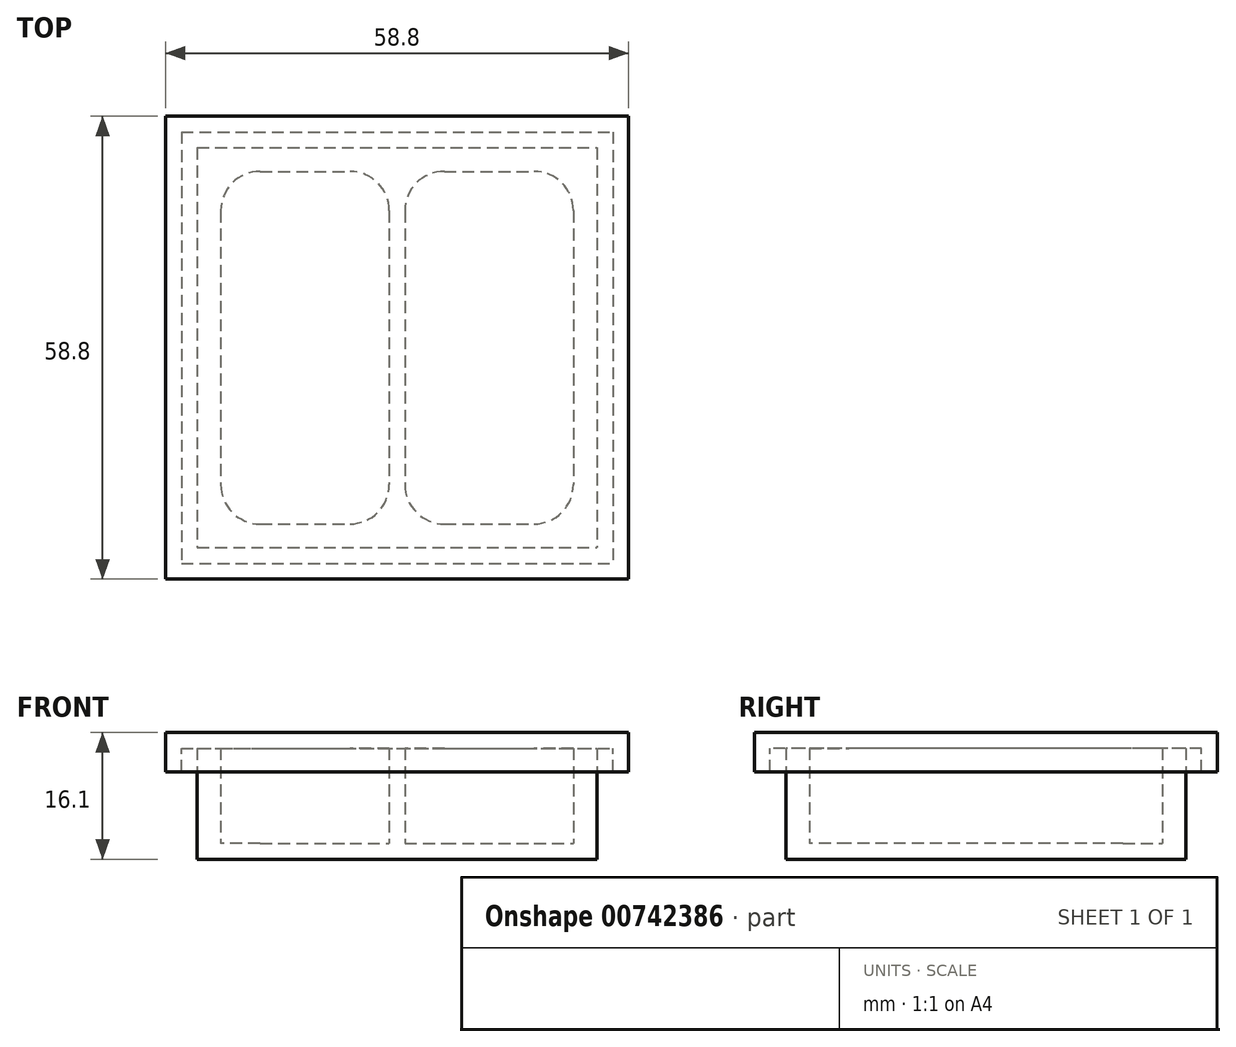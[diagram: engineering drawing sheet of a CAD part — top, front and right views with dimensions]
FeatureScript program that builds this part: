
annotation { "Feature Type Name" : "Feature", "Feature Type Description" : "" }
export const myFeature = defineFeature(function(context is Context, id is Id, definition is map)
    precondition{}
    {
        {
            var Q0;
            Q0=qCreatedBy(makeId("Top.planeOp"),FACE);
            var sketch = newSketch(context, id + "F0", { "sketchPlane" : qUnion([Q0])});
            skLineSegment(sketch, "E0.bottom", {"start": v(-30.87, 24.78) * mm, "end": v(19.93, 24.78) * mm});
            skLineSegment(sketch, "E0.top", {"start": v(-30.87, -26.02) * mm, "end": v(19.93, -26.02) * mm});
            skLineSegment(sketch, "E0.left", {"start": v(-30.87, 24.78) * mm, "end": v(-30.87, -26.02) * mm});
            skLineSegment(sketch, "E0.right", {"start": v(19.93, 24.78) * mm, "end": v(19.93, -26.02) * mm});
            skLineSegment(sketch, "E1.0", {"start": v(-27.87, 21.78) * mm, "end": v(16.93, 21.78) * mm});
            skLineSegment(sketch, "E1.1", {"start": v(-27.87, 21.78) * mm, "end": v(-27.87, 12.83) * mm});
            skLineSegment(sketch, "E1.2", {"start": v(-27.87, -23.02) * mm, "end": v(16.93, -23.02) * mm});
            skLineSegment(sketch, "E1.3", {"start": v(16.93, 21.78) * mm, "end": v(16.93, 12.83) * mm});
            skLineSegment(sketch, "E2", {"start": v(-6.47, -14.07) * mm, "end": v(-4.47, -14.07) * mm});
            skLineSegment(sketch, "E3", {"start": v(-6.47, -11.07) * mm, "end": v(-4.47, -11.07) * mm});
            skLineSegment(sketch, "E4", {"start": v(-6.47, -2.12) * mm, "end": v(-4.47, -2.12) * mm});
            skLineSegment(sketch, "E5", {"start": v(-6.47, 0.88) * mm, "end": v(-4.47, 0.88) * mm});
            skLineSegment(sketch, "E6", {"start": v(-6.47, 9.83) * mm, "end": v(-4.47, 9.83) * mm});
            skLineSegment(sketch, "E7", {"start": v(-6.47, 12.83) * mm, "end": v(-4.47, 12.83) * mm});
            skPoint(sketch, "E8.endSnap0", {"position": v(-5.47, -14.07) * mm});
            skLineSegment(sketch, "E9.trimOffspring", {"start": v(-27.87, -14.07) * mm, "end": v(-27.87, -23.02) * mm});
            skLineSegment(sketch, "E10.trimOffspring", {"start": v(16.93, -14.07) * mm, "end": v(16.93, -23.02) * mm});
            skLineSegment(sketch, "E11.trimOffspring", {"start": v(-27.87, -2.12) * mm, "end": v(-27.87, -11.07) * mm});
            skLineSegment(sketch, "E12.trimOffspring", {"start": v(16.93, 9.83) * mm, "end": v(16.93, 0.88) * mm});
            skLineSegment(sketch, "E13.trimOffspring", {"start": v(-27.87, 9.83) * mm, "end": v(-27.87, 0.88) * mm});
            skLineSegment(sketch, "E14", {"start": v(16.93, -11.07) * mm, "end": v(16.93, -2.12) * mm});
            skLineSegment(sketch, "E15", {"start": v(-5.47, -23.02) * mm, "end": v(-5.47, 21.78) * mm});
            skLineSegment(sketch, "E16", {"start": v(-6.47, 21.78) * mm, "end": v(-6.47, -23.02) * mm});
            skLineSegment(sketch, "E17", {"start": v(-4.47, 21.78) * mm, "end": v(-4.47, -23.02) * mm});
            skPoint(sketch, "E8.end.orphan", {"position": v(8.71, -14.07) * mm});
            skLineSegment(sketch, "E18", {"start": v(-27.87, -14.07) * mm, "end": v(-27.87, -11.07) * mm});
            skLineSegment(sketch, "E19", {"start": v(-27.87, -2.12) * mm, "end": v(-27.87, 0.88) * mm});
            skLineSegment(sketch, "E20", {"start": v(-27.87, 9.83) * mm, "end": v(-27.87, 12.83) * mm});
            skLineSegment(sketch, "E21", {"start": v(16.93, 9.83) * mm, "end": v(16.93, 12.83) * mm});
            skLineSegment(sketch, "E22", {"start": v(16.93, -2.12) * mm, "end": v(16.93, 0.88) * mm});
            skLineSegment(sketch, "E23", {"start": v(16.93, -14.07) * mm, "end": v(16.93, -11.07) * mm});
            skSolve(sketch);
        }
        {
            var Q0;
            Q0=makeQuery(id+"F0.imprint","IMPRINT",FACE,{"disambiguationData":[TD([[makeQuery(id+"F0.imprint","IMPRINT",EDGE,{"derivedFrom":sQuery(id+"F0.wireOp",EDGE,"E0.bottom")}),-1.0]])]});
            var Q1;
            {var subQ0=sQuery(id+"F0.wireOp",EDGE,"E16");var subQ1=sQuery(id+"F0.wireOp",EDGE,"E3");var subQ2=makeQuery(id+"F0.imprint","INTERSECT",VERTEX,{"derivedFrom":[subQ1,subQ0]});Q1=makeQuery(id+"F0.imprint","IMPRINT",FACE,{"disambiguationData":[TD([[makeQuery(id+"F0.imprint","IMPRINT",EDGE,{"disambiguationData":[TD([[subQ2,-1.0]])],"derivedFrom":subQ1}),1.0]])]});}
            var Q2;
            {var subQ0=sQuery(id+"F0.wireOp",EDGE,"E15");var subQ1=sQuery(id+"F0.wireOp",EDGE,"E3");var subQ2=makeQuery(id+"F0.imprint","INTERSECT",VERTEX,{"derivedFrom":[subQ1,subQ0]});Q2=makeQuery(id+"F0.imprint","IMPRINT",FACE,{"disambiguationData":[TD([[makeQuery(id+"F0.imprint","IMPRINT",EDGE,{"disambiguationData":[TD([[subQ2,-1.0]])],"derivedFrom":subQ1}),1.0]])]});}
            var Q3;
            {var subQ0=sQuery(id+"F0.wireOp",EDGE,"E16");var subQ1=sQuery(id+"F0.wireOp",EDGE,"E2");var subQ2=makeQuery(id+"F0.imprint","INTERSECT",VERTEX,{"derivedFrom":[subQ1,subQ0]});Q3=makeQuery(id+"F0.imprint","IMPRINT",FACE,{"disambiguationData":[TD([[makeQuery(id+"F0.imprint","IMPRINT",EDGE,{"disambiguationData":[TD([[subQ2,-1.0]])],"derivedFrom":subQ1}),1.0]])]});}
            var Q4;
            {var subQ0=sQuery(id+"F0.wireOp",EDGE,"E15");var subQ1=sQuery(id+"F0.wireOp",EDGE,"E2");var subQ2=makeQuery(id+"F0.imprint","INTERSECT",VERTEX,{"derivedFrom":[subQ1,subQ0]});Q4=makeQuery(id+"F0.imprint","IMPRINT",FACE,{"disambiguationData":[TD([[makeQuery(id+"F0.imprint","IMPRINT",EDGE,{"disambiguationData":[TD([[subQ2,-1.0]])],"derivedFrom":subQ1}),1.0]])]});}
            var Q5;
            {var subQ0=sQuery(id+"F0.wireOp",EDGE,"E15");var subQ1=sQuery(id+"F0.wireOp",EDGE,"E1.2");var subQ2=makeQuery(id+"F0.imprint","INTERSECT",VERTEX,{"derivedFrom":[subQ1,subQ0]});Q5=makeQuery(id+"F0.imprint","IMPRINT",FACE,{"disambiguationData":[TD([[makeQuery(id+"F0.imprint","IMPRINT",EDGE,{"disambiguationData":[TD([[subQ2,1.0]])],"derivedFrom":subQ1}),1.0]])]});}
            var Q6;
            {var subQ0=sQuery(id+"F0.wireOp",EDGE,"E15");var subQ1=sQuery(id+"F0.wireOp",EDGE,"E1.2");var subQ2=makeQuery(id+"F0.imprint","INTERSECT",VERTEX,{"derivedFrom":[subQ1,subQ0]});Q6=makeQuery(id+"F0.imprint","IMPRINT",FACE,{"disambiguationData":[TD([[makeQuery(id+"F0.imprint","IMPRINT",EDGE,{"disambiguationData":[TD([[subQ2,-1.0]])],"derivedFrom":subQ1}),1.0]])]});}
            var Q7;
            {var subQ0=sQuery(id+"F0.wireOp",EDGE,"E16");var subQ1=sQuery(id+"F0.wireOp",EDGE,"E4");var subQ2=makeQuery(id+"F0.imprint","INTERSECT",VERTEX,{"derivedFrom":[subQ1,subQ0]});Q7=makeQuery(id+"F0.imprint","IMPRINT",FACE,{"disambiguationData":[TD([[makeQuery(id+"F0.imprint","IMPRINT",EDGE,{"disambiguationData":[TD([[subQ2,-1.0]])],"derivedFrom":subQ1}),1.0]])]});}
            var Q8;
            {var subQ0=sQuery(id+"F0.wireOp",EDGE,"E15");var subQ1=sQuery(id+"F0.wireOp",EDGE,"E4");var subQ2=makeQuery(id+"F0.imprint","INTERSECT",VERTEX,{"derivedFrom":[subQ1,subQ0]});Q8=makeQuery(id+"F0.imprint","IMPRINT",FACE,{"disambiguationData":[TD([[makeQuery(id+"F0.imprint","IMPRINT",EDGE,{"disambiguationData":[TD([[subQ2,-1.0]])],"derivedFrom":subQ1}),1.0]])]});}
            var Q9;
            {var subQ0=sQuery(id+"F0.wireOp",EDGE,"E16");var subQ1=sQuery(id+"F0.wireOp",EDGE,"E5");var subQ2=makeQuery(id+"F0.imprint","INTERSECT",VERTEX,{"derivedFrom":[subQ1,subQ0]});Q9=makeQuery(id+"F0.imprint","IMPRINT",FACE,{"disambiguationData":[TD([[makeQuery(id+"F0.imprint","IMPRINT",EDGE,{"disambiguationData":[TD([[subQ2,-1.0]])],"derivedFrom":subQ1}),1.0]])]});}
            var Q10;
            {var subQ0=sQuery(id+"F0.wireOp",EDGE,"E15");var subQ1=sQuery(id+"F0.wireOp",EDGE,"E5");var subQ2=makeQuery(id+"F0.imprint","INTERSECT",VERTEX,{"derivedFrom":[subQ1,subQ0]});Q10=makeQuery(id+"F0.imprint","IMPRINT",FACE,{"disambiguationData":[TD([[makeQuery(id+"F0.imprint","IMPRINT",EDGE,{"disambiguationData":[TD([[subQ2,-1.0]])],"derivedFrom":subQ1}),1.0]])]});}
            var Q11;
            {var subQ0=sQuery(id+"F0.wireOp",EDGE,"E15");var subQ1=sQuery(id+"F0.wireOp",EDGE,"E1.0");var subQ2=makeQuery(id+"F0.imprint","INTERSECT",VERTEX,{"derivedFrom":[subQ1,subQ0]});Q11=makeQuery(id+"F0.imprint","IMPRINT",FACE,{"disambiguationData":[TD([[makeQuery(id+"F0.imprint","IMPRINT",EDGE,{"disambiguationData":[TD([[subQ2,1.0]])],"derivedFrom":subQ1}),-1.0]])]});}
            var Q12;
            {var subQ0=sQuery(id+"F0.wireOp",EDGE,"E15");var subQ1=sQuery(id+"F0.wireOp",EDGE,"E1.0");var subQ2=makeQuery(id+"F0.imprint","INTERSECT",VERTEX,{"derivedFrom":[subQ1,subQ0]});Q12=makeQuery(id+"F0.imprint","IMPRINT",FACE,{"disambiguationData":[TD([[makeQuery(id+"F0.imprint","IMPRINT",EDGE,{"disambiguationData":[TD([[subQ2,-1.0]])],"derivedFrom":subQ1}),-1.0]])]});}
            var Q13;
            {var subQ0=sQuery(id+"F0.wireOp",EDGE,"E16");var subQ1=sQuery(id+"F0.wireOp",EDGE,"E6");var subQ2=makeQuery(id+"F0.imprint","INTERSECT",VERTEX,{"derivedFrom":[subQ1,subQ0]});Q13=makeQuery(id+"F0.imprint","IMPRINT",FACE,{"disambiguationData":[TD([[makeQuery(id+"F0.imprint","IMPRINT",EDGE,{"disambiguationData":[TD([[subQ2,-1.0]])],"derivedFrom":subQ1}),1.0]])]});}
            var Q14;
            {var subQ0=sQuery(id+"F0.wireOp",EDGE,"E15");var subQ1=sQuery(id+"F0.wireOp",EDGE,"E6");var subQ2=makeQuery(id+"F0.imprint","INTERSECT",VERTEX,{"derivedFrom":[subQ1,subQ0]});Q14=makeQuery(id+"F0.imprint","IMPRINT",FACE,{"disambiguationData":[TD([[makeQuery(id+"F0.imprint","IMPRINT",EDGE,{"disambiguationData":[TD([[subQ2,-1.0]])],"derivedFrom":subQ1}),1.0]])]});}
            extrude(context, id + "F1", {"entities" : qUnion([Q0, Q1, Q2, Q3, Q4, Q5, Q6, Q7, Q8, Q9, Q10, Q11, Q12, Q13, Q14]), "depth" : 15 * mm, "offsetDistance" : 25 * mm});
        }
        {
            var Q0;
            {var subQ0=sQuery(id+"F0.wireOp",EDGE,"E9.trimOffspring");Q0=makeQuery(id+"F0.imprint","IMPRINT",FACE,{"disambiguationData":[TD([[makeQuery(id+"F0.imprint","IMPRINT",EDGE,{"derivedFrom":subQ0}),1.0]])]});}
            var Q1;
            {var subQ0=sQuery(id+"F0.wireOp",EDGE,"E10.trimOffspring");Q1=makeQuery(id+"F0.imprint","IMPRINT",FACE,{"disambiguationData":[TD([[makeQuery(id+"F0.imprint","IMPRINT",EDGE,{"derivedFrom":subQ0}),-1.0]])]});}
            var Q2;
            {var subQ0=sQuery(id+"F0.wireOp",EDGE,"E11.trimOffspring");Q2=makeQuery(id+"F0.imprint","IMPRINT",FACE,{"disambiguationData":[TD([[makeQuery(id+"F0.imprint","IMPRINT",EDGE,{"derivedFrom":subQ0}),1.0]])]});}
            var Q3;
            {var subQ0=sQuery(id+"F0.wireOp",EDGE,"E14");Q3=makeQuery(id+"F0.imprint","IMPRINT",FACE,{"disambiguationData":[TD([[makeQuery(id+"F0.imprint","IMPRINT",EDGE,{"derivedFrom":subQ0}),1.0]])]});}
            var Q4;
            {var subQ0=sQuery(id+"F0.wireOp",EDGE,"E13.trimOffspring");Q4=makeQuery(id+"F0.imprint","IMPRINT",FACE,{"disambiguationData":[TD([[makeQuery(id+"F0.imprint","IMPRINT",EDGE,{"derivedFrom":subQ0}),1.0]])]});}
            var Q5;
            {var subQ0=sQuery(id+"F0.wireOp",EDGE,"E12.trimOffspring");Q5=makeQuery(id+"F0.imprint","IMPRINT",FACE,{"disambiguationData":[TD([[makeQuery(id+"F0.imprint","IMPRINT",EDGE,{"derivedFrom":subQ0}),-1.0]])]});}
            var Q6;
            {var subQ0=sQuery(id+"F0.wireOp",EDGE,"E1.1");Q6=makeQuery(id+"F0.imprint","IMPRINT",FACE,{"disambiguationData":[TD([[makeQuery(id+"F0.imprint","IMPRINT",EDGE,{"derivedFrom":subQ0}),1.0]])]});}
            var Q7;
            {var subQ0=sQuery(id+"F0.wireOp",EDGE,"E1.3");Q7=makeQuery(id+"F0.imprint","IMPRINT",FACE,{"disambiguationData":[TD([[makeQuery(id+"F0.imprint","IMPRINT",EDGE,{"derivedFrom":subQ0}),-1.0]])]});}
            extrude(context, id + "F2", {"entities" : qUnion([Q0, Q1, Q2, Q3, Q4, Q5, Q6, Q7]), "operationType" : NewBodyOperationType.ADD, "depth" : 2 * mm, "offsetDistance" : 25 * mm});
        }
        {
            var Q0;
            Q0=makeQuery(id+"F1.opExtrude","SWEPT_EDGE",EDGE,{"disambiguationData":[OSD([sQuery(id+"F0.wireOp",EDGE,"E1.2"),sQuery(id+"F0.wireOp",EDGE,"E9.trimOffspring")])]});
            var Q1;
            Q1=makeQuery(id+"F1.opExtrude","SWEPT_EDGE",EDGE,{"disambiguationData":[OSD([sQuery(id+"F0.wireOp",EDGE,"E1.2"),sQuery(id+"F0.wireOp",EDGE,"E10.trimOffspring")])]});
            var Q2;
            Q2=makeQuery(id+"F1.opExtrude","SWEPT_EDGE",EDGE,{"disambiguationData":[OSD([sQuery(id+"F0.wireOp",EDGE,"E2"),sQuery(id+"F0.wireOp",EDGE,"E10.trimOffspring")])]});
            var Q3;
            Q3=makeQuery(id+"F1.opExtrude","SWEPT_EDGE",EDGE,{"disambiguationData":[OSD([sQuery(id+"F0.wireOp",EDGE,"E2"),sQuery(id+"F0.wireOp",EDGE,"E9.trimOffspring")])]});
            var Q4;
            Q4=makeQuery(id+"F1.opExtrude","SWEPT_EDGE",EDGE,{"disambiguationData":[OSD([sQuery(id+"F0.wireOp",EDGE,"E3"),sQuery(id+"F0.wireOp",EDGE,"E11.trimOffspring")])]});
            var Q5;
            Q5=makeQuery(id+"F1.opExtrude","SWEPT_EDGE",EDGE,{"disambiguationData":[OSD([sQuery(id+"F0.wireOp",EDGE,"E5"),sQuery(id+"F0.wireOp",EDGE,"E13.trimOffspring")])]});
            var Q6;
            Q6=makeQuery(id+"F1.opExtrude","SWEPT_EDGE",EDGE,{"disambiguationData":[OSD([sQuery(id+"F0.wireOp",EDGE,"E1.1"),sQuery(id+"F0.wireOp",EDGE,"E7")])]});
            var Q7;
            Q7=makeQuery(id+"F1.opExtrude","SWEPT_EDGE",EDGE,{"disambiguationData":[OSD([sQuery(id+"F0.wireOp",EDGE,"E6"),sQuery(id+"F0.wireOp",EDGE,"E13.trimOffspring")])]});
            var Q8;
            Q8=makeQuery(id+"F1.opExtrude","SWEPT_EDGE",EDGE,{"disambiguationData":[OSD([sQuery(id+"F0.wireOp",EDGE,"E1.0"),sQuery(id+"F0.wireOp",EDGE,"E1.1")])]});
            var Q9;
            Q9=makeQuery(id+"F1.opExtrude","SWEPT_EDGE",EDGE,{"disambiguationData":[OSD([sQuery(id+"F0.wireOp",EDGE,"E1.0"),sQuery(id+"F0.wireOp",EDGE,"E1.3")])]});
            var Q10;
            Q10=makeQuery(id+"F1.opExtrude","SWEPT_EDGE",EDGE,{"disambiguationData":[OSD([sQuery(id+"F0.wireOp",EDGE,"E6"),sQuery(id+"F0.wireOp",EDGE,"E12.trimOffspring")])]});
            var Q11;
            Q11=makeQuery(id+"F1.opExtrude","SWEPT_EDGE",EDGE,{"disambiguationData":[OSD([sQuery(id+"F0.wireOp",EDGE,"E4"),sQuery(id+"F0.wireOp",EDGE,"E14")])]});
            var Q12;
            Q12=makeQuery(id+"F1.opExtrude","SWEPT_EDGE",EDGE,{"disambiguationData":[OSD([sQuery(id+"F0.wireOp",EDGE,"E5"),sQuery(id+"F0.wireOp",EDGE,"E12.trimOffspring")])]});
            var Q13;
            Q13=makeQuery(id+"F1.opExtrude","SWEPT_EDGE",EDGE,{"disambiguationData":[OSD([sQuery(id+"F0.wireOp",EDGE,"E1.3"),sQuery(id+"F0.wireOp",EDGE,"E7")])]});
            var Q14;
            Q14=makeQuery(id+"F1.opExtrude","SWEPT_EDGE",EDGE,{"disambiguationData":[OSD([sQuery(id+"F0.wireOp",EDGE,"E3"),sQuery(id+"F0.wireOp",EDGE,"E14")])]});
            var Q15;
            Q15=makeQuery(id+"F1.opExtrude","SWEPT_EDGE",EDGE,{"disambiguationData":[OSD([sQuery(id+"F0.wireOp",EDGE,"E1.0"),sQuery(id+"F0.wireOp",EDGE,"E17")])]});
            var Q16;
            Q16=makeQuery(id+"F1.opExtrude","SWEPT_EDGE",EDGE,{"disambiguationData":[OSD([sQuery(id+"F0.wireOp",EDGE,"E1.0"),sQuery(id+"F0.wireOp",EDGE,"E16")])]});
            var Q17;
            Q17=makeQuery(id+"F1.opExtrude","SWEPT_EDGE",EDGE,{"disambiguationData":[OSD([sQuery(id+"F0.wireOp",EDGE,"E1.2"),sQuery(id+"F0.wireOp",EDGE,"E16")])]});
            var Q18;
            Q18=makeQuery(id+"F1.opExtrude","SWEPT_EDGE",EDGE,{"disambiguationData":[OSD([sQuery(id+"F0.wireOp",EDGE,"E1.2"),sQuery(id+"F0.wireOp",EDGE,"E17")])]});
            fillet(context, id + "F3", {"entities" : qUnion([Q0, Q1, Q2, Q3, Q4, Q5, Q6, Q7, Q8, Q9, Q10, Q11, Q12, Q13, Q14, Q15, Q16, Q17, Q18]), "radius" : 5 * mm, "tangentPropagation" : true, "allowEdgeOverflow" : false});
        }
        {
            var Q0;
            Q0=qCreatedBy(makeId("Top.planeOp"),FACE);
            cPlane(context, id + "F4", {"entities" : qUnion([Q0]), "cplaneType" : CPlaneType.OFFSET, "offset" : 16.1 * mm, "width" : 150 * mm, "height" : 150 * mm});
        }
        {
            var Q0;
            Q0=qCreatedBy(id+"F4.planeOp",FACE);
            var sketch = newSketch(context, id + "F5", { "sketchPlane" : qUnion([Q0])});
            skLineSegment(sketch, "E24.0", {"start": v(-30.87, 24.78) * mm, "end": v(-30.87, -26.02) * mm});
            skLineSegment(sketch, "E25.0", {"start": v(-30.87, 24.78) * mm, "end": v(19.93, 24.78) * mm});
            skLineSegment(sketch, "E26.0", {"start": v(19.93, 24.78) * mm, "end": v(19.93, -26.02) * mm});
            skLineSegment(sketch, "E27.bottom", {"start": v(-32.87, 26.78) * mm, "end": v(21.93, 26.78) * mm});
            skLineSegment(sketch, "E27.top", {"start": v(-32.87, -28.02) * mm, "end": v(21.93, -28.02) * mm});
            skLineSegment(sketch, "E27.left", {"start": v(-32.87, 26.78) * mm, "end": v(-32.87, -28.02) * mm});
            skLineSegment(sketch, "E27.right", {"start": v(21.93, 26.78) * mm, "end": v(21.93, -28.02) * mm});
            skLineSegment(sketch, "E28", {"start": v(19.93, -26.02) * mm, "end": v(-30.87, -26.02) * mm});
            skLineSegment(sketch, "E29.bottom", {"start": v(-34.87, 28.78) * mm, "end": v(23.93, 28.78) * mm});
            skLineSegment(sketch, "E29.top", {"start": v(-34.87, -30.02) * mm, "end": v(23.93, -30.02) * mm});
            skLineSegment(sketch, "E29.left", {"start": v(-34.87, 28.78) * mm, "end": v(-34.87, -30.02) * mm});
            skLineSegment(sketch, "E29.right", {"start": v(23.93, 28.78) * mm, "end": v(23.93, -30.02) * mm});
            skSolve(sketch);
        }
        {
            var Q0;
            Q0=makeQuery(id+"F5.imprint","IMPRINT",FACE,{"disambiguationData":[TD([[makeQuery(id+"F5.imprint","IMPRINT",EDGE,{"derivedFrom":sQuery(id+"F5.wireOp",EDGE,"E27.bottom")}),1.0]])]});
            extrude(context, id + "F6", {"entities" : qUnion([Q0]), "oppositeDirection" : true, "depth" : 5 * mm, "offsetDistance" : 25 * mm});
        }
        {
            var Q0;
            Q0=makeQuery(id+"F5.imprint","IMPRINT",FACE,{"disambiguationData":[TD([[makeQuery(id+"F5.imprint","IMPRINT",EDGE,{"derivedFrom":sQuery(id+"F5.wireOp",EDGE,"E24.0")}),1.0]])]});
            var Q1;
            Q1=makeQuery(id+"F5.imprint","IMPRINT",FACE,{"disambiguationData":[TD([[makeQuery(id+"F5.imprint","IMPRINT",EDGE,{"derivedFrom":sQuery(id+"F5.wireOp",EDGE,"E24.0")}),-1.0]])]});
            extrude(context, id + "F7", {"entities" : qUnion([Q0, Q1]), "operationType" : NewBodyOperationType.ADD, "oppositeDirection" : true, "depth" : 2 * mm, "offsetDistance" : 25 * mm});
        }
    });
